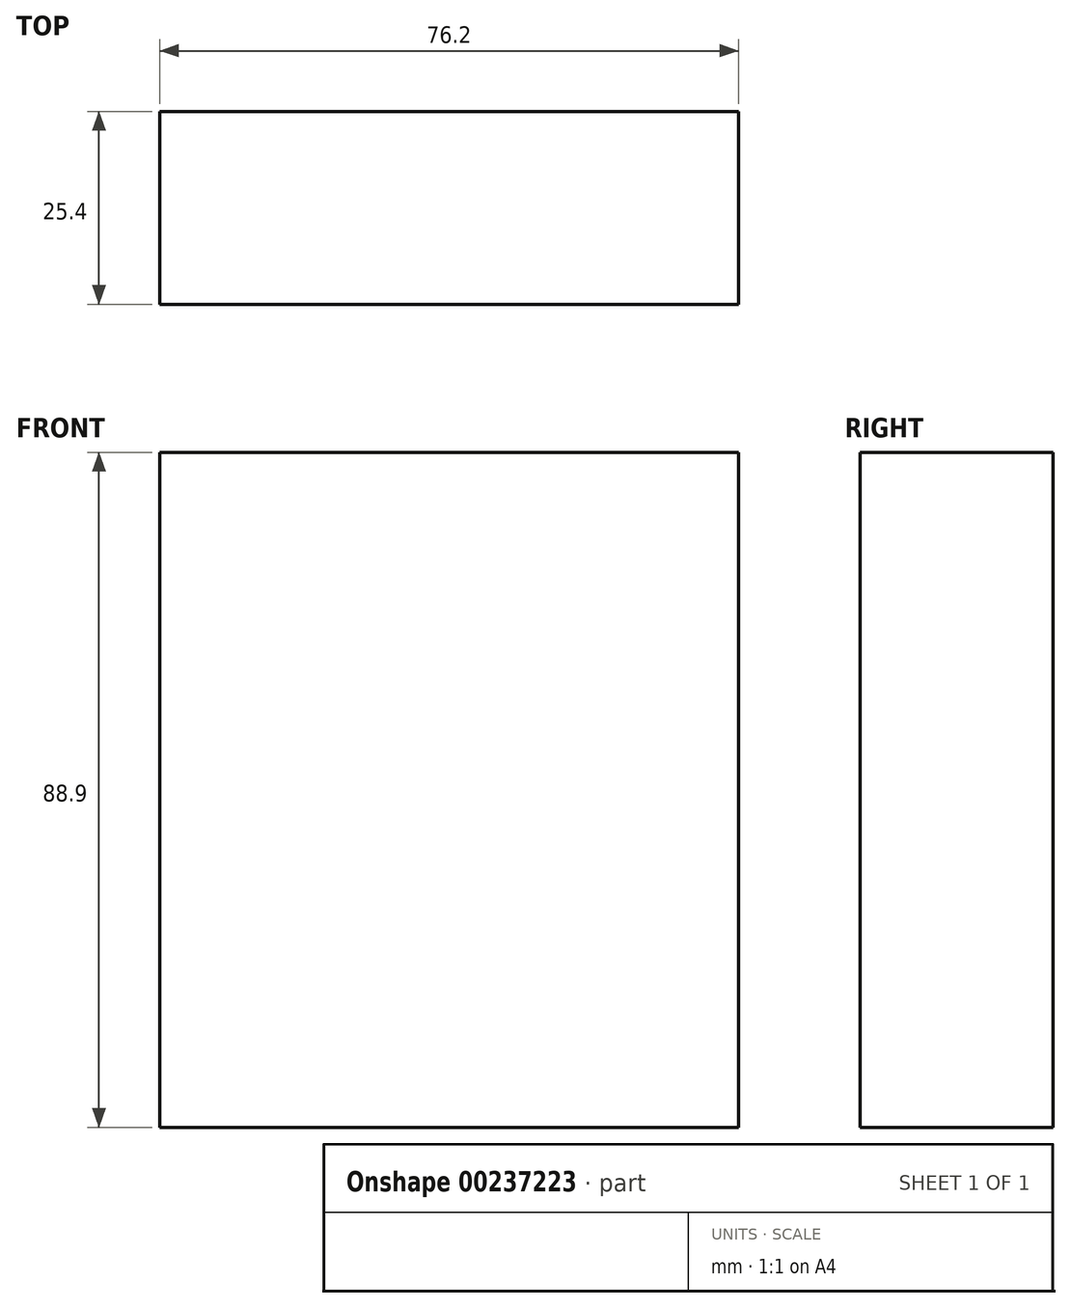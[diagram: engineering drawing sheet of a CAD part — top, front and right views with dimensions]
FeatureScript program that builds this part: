
annotation { "Feature Type Name" : "Feature", "Feature Type Description" : "" }
export const myFeature = defineFeature(function(context is Context, id is Id, definition is map)
    precondition{}
    {
        {
            var Q0;
            Q0=qCreatedBy(makeId("Front.planeOp"),FACE);
            var sketch = newSketch(context, id + "F0", { "sketchPlane" : qUnion([Q0])});
            skLineSegment(sketch, "E0.bottom", {"start": v(-39.89, 38.44) * mm, "end": v(36.31, 38.44) * mm});
            skLineSegment(sketch, "E0.top", {"start": v(-39.89, -50.46) * mm, "end": v(36.31, -50.46) * mm});
            skLineSegment(sketch, "E0.left", {"start": v(-39.89, 38.44) * mm, "end": v(-39.89, -50.46) * mm});
            skLineSegment(sketch, "E0.right", {"start": v(36.31, 38.44) * mm, "end": v(36.31, -50.46) * mm});
            skSolve(sketch);
        }
        {
            var Q0;
            Q0 = qSketchRegion(id + "F0", true);
            extrude(context, id + "F1", {"entities" : qUnion([Q0]), "depth" : 25.4 * mm});
        }
    });
